# Revit family: Go basin 450rfa
name_source: partatom
category: Furniture
units: mm (PartAtom-declared; Revit-internal decimal feet)

## family parameters
Always vertical = Yes
Cut with Voids When Loaded = No
OmniClass Number = 23.40.20.00
OmniClass Title = General Furniture and Specialties
Room Calculation Point = No
Shared = No
Work Plane-Based = No

## types (1)
- Go 450 basin
    Article number = 1273186
    Back to bowl = 110 mm  [stored 0.360892 ft]
    Back to tap hole = 45 mm  [stored 0.147638 ft]
    Back to waste hole = 190 mm
    Basin depth = 310 mm  [stored 1.01706 ft]
    Bowl depth = 170 mm  [stored 0.557743 ft]
    Bowl inner width = 340 mm  [stored 1.11549 ft]
    GTIN = 7330027103723
    Manufacturer = Hafa Bathroom Group AB
    Material finish = Porcelain
    Model = Rektangular ho 600
    URL = www.hafa.se
    Width basin = 450 mm  [stored 1.47638 ft]

note: [stored X ft] marks values corroborated as IEEE doubles in the binary element streams (Revit-internal decimal feet)

## geometry (parser evidence)
native form markers: Sweep x2
no freeform markers — native parametric forms only
